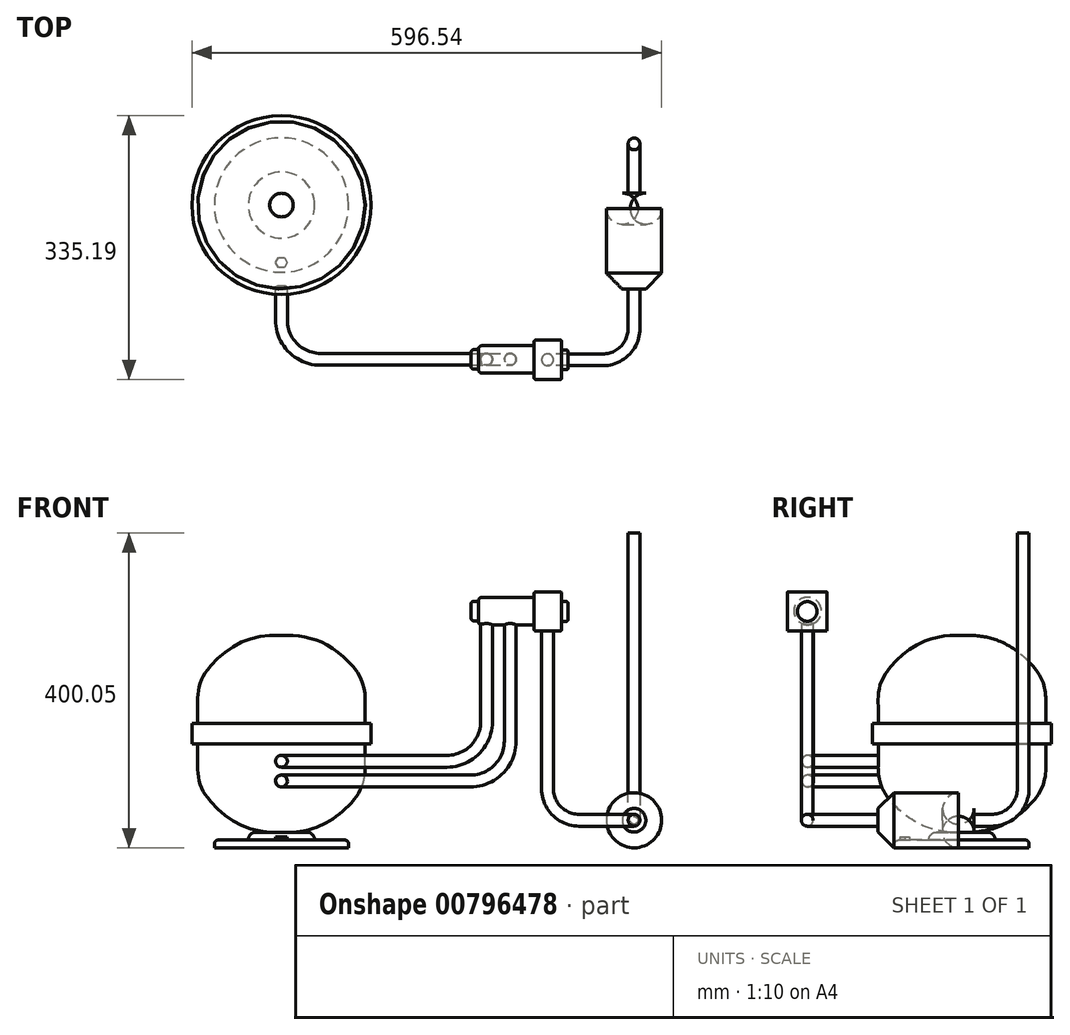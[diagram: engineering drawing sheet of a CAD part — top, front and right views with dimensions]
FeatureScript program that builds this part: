
annotation { "Feature Type Name" : "Feature", "Feature Type Description" : "" }
export const myFeature = defineFeature(function(context is Context, id is Id, definition is map)
    precondition{}
    {
        {
            var Q0;
            Q0=qCreatedBy(makeId("Front.planeOp"),FACE);
            var sketch = newSketch(context, id + "F0", { "sketchPlane" : qUnion([Q0])});
            skLineSegment(sketch, "E0", {"start": v(0, 125) * mm, "end": v(0, 0) * mm});
            skLineSegment(sketch, "E1", {"start": v(0, 125) * mm, "end": v(15, 125) * mm});
            skFitSpline(sketch, "E2", {"points": [v(15, 125) * mm, v(59.48, 111.76) * mm, v(101.6, 68.43) * mm, v(106.42, 35.93) * mm, v(106.42, 13.06) * mm], "startDerivative": vector(170.56, -15.33) * mm, "endDerivative": vector(0, -154.1) * mm});
            skLineSegment(sketch, "E3", {"start": v(106.42, 13.06) * mm, "end": v(113.64, 13.06) * mm});
            skLineSegment(sketch, "E4", {"start": v(113.64, 13.06) * mm, "end": v(113.64, 0) * mm});
            skLineSegment(sketch, "E5", {"start": v(0, 0) * mm, "end": v(113.64, 0) * mm});
            skFitSpline(sketch, "E6.MirrorCS", {"points": [v(15, -125) * mm, v(59.48, -111.76) * mm, v(101.6, -68.43) * mm, v(106.42, -35.93) * mm, v(106.42, -13.06) * mm], "startDerivative": vector(170.56, 15.33) * mm, "endDerivative": vector(0, 154.1) * mm});
            skLineSegment(sketch, "E7.MirrorCS", {"start": v(0, -125) * mm, "end": v(15, -125) * mm});
            skLineSegment(sketch, "E8.MirrorCS", {"start": v(0, -125) * mm, "end": v(0, 0) * mm});
            skLineSegment(sketch, "E9.MirrorCS", {"start": v(106.42, -13.06) * mm, "end": v(113.64, -13.06) * mm});
            skLineSegment(sketch, "E10.MirrorCS", {"start": v(113.64, -13.06) * mm, "end": v(113.64, 0) * mm});
            skPoint(sketch, "E11.MirrorCS.start.orphan", {"position": v(-15, 125) * mm});
            skPoint(sketch, "E12.MirrorCS.start.orphan", {"position": v(0, 125) * mm});
            skSolve(sketch);
        }
        {
            var Q0;
            Q0=makeQuery(id+"F0.imprint","IMPRINT",FACE,{"disambiguationData":[TD([[makeQuery(id+"F0.imprint","IMPRINT",EDGE,{"derivedFrom":sQuery(id+"F0.wireOp",EDGE,"E0")}),1.0]])]});
            var Q1;
            Q1=makeQuery(id+"F0.imprint","IMPRINT",FACE,{"disambiguationData":[TD([[makeQuery(id+"F0.imprint","IMPRINT",EDGE,{"derivedFrom":sQuery(id+"F0.wireOp",EDGE,"E5")}),-1.0]])]});
            var Q2;
            Q2=sQuery(id+"F0.wireOp",EDGE,"E0");
            revolve(context, id + "F1", {"surfaceOperationType" : NewSurfaceOperationType.NEW, "entities" : qUnion([Q0, Q1]), "axis" : qUnion([Q2]), "revolveType" : RevolveType.FULL});
        }
        {
            var Q0;
            Q0=makeQuery(id+"F1.opRevolve","SWEPT_FACE",FACE,{"disambiguationData":[OSD([sQuery(id+"F0.wireOp",EDGE,"E7.MirrorCS")])]});
            var sketch = newSketch(context, id + "F2", { "sketchPlane" : qUnion([Q0])});
            skCircle(sketch, "E13", {"center": v(0, 0) * mm, "radius": 42.2 * mm});
            skSolve(sketch);
        }
        {
            var Q0;
            Q0 = qSketchRegion(id + "F2", true);
            extrude(context, id + "F3", {"entities" : qUnion([Q0]), "operationType" : NewBodyOperationType.ADD, "depth" : 10 * mm, "offsetDistance" : 25 * mm});
        }
        {
            var Q0;
            Q0=makeQuery(id+"F3.opExtrude","CAP_FACE",FACE,{"disambiguationData":[OSD([sQuery(id+"F2.wireOp",EDGE,"E13")])],"isStart":false});
            var sketch = newSketch(context, id + "F4", { "sketchPlane" : qUnion([Q0])});
            skCircle(sketch, "E14", {"center": v(0, 0) * mm, "radius": 85.28 * mm});
            skSolve(sketch);
        }
        {
            var Q0;
            Q0 = qSketchRegion(id + "F4", true);
            extrude(context, id + "F5", {"entities" : qUnion([Q0]), "operationType" : NewBodyOperationType.ADD, "depth" : 10 * mm, "offsetDistance" : 25 * mm});
        }
        {
            var Q0;
            Q0=makeQuery(id+"F3.opExtrude","CAP_EDGE",EDGE,{"disambiguationData":[OSD([sQuery(id+"F2.wireOp",EDGE,"E13")])],"isStart":false});
            var Q1;
            Q1=makeQuery(id+"F5.opExtrude","CAP_EDGE",EDGE,{"disambiguationData":[OSD([sQuery(id+"F4.wireOp",EDGE,"E14")])],"isStart":true});
            fillet(context, id + "F6", {"entities" : qUnion([Q0, Q1]), "radius" : 5 * mm, "tangentPropagation" : true, "allowEdgeOverflow" : false});
        }
        {
            var Q0;
            Q0=makeQuery(id+"F3.opExtrude","CAP_EDGE",EDGE,{"disambiguationData":[OSD([sQuery(id+"F2.wireOp",EDGE,"E13")])],"isStart":true});
            fillet(context, id + "F7", {"entities" : qUnion([Q0]), "radius" : 10 * mm, "tangentPropagation" : true, "allowEdgeOverflow" : false});
        }
        {
            var Q0;
            Q0=makeQuery(id+"F5.opExtrude","CAP_FACE",FACE,{"disambiguationData":[OSD([sQuery(id+"F4.wireOp",EDGE,"E14")])],"isStart":true});
            var sketch = newSketch(context, id + "F8", { "sketchPlane" : qUnion([Q0])});
            skCircle(sketch, "E15.cCircle", {"center": v(0, -72.8) * mm, "radius": 6.33 * mm, "construction": true});
            skLineSegment(sketch, "E15.0", {"start": v(-3.65, -66.47) * mm, "end": v(3.65, -66.47) * mm});
            skLineSegment(sketch, "E15.1", {"start": v(3.65, -66.47) * mm, "end": v(7.3, -72.8) * mm});
            skLineSegment(sketch, "E15.2", {"start": v(7.3, -72.8) * mm, "end": v(3.65, -79.13) * mm});
            skLineSegment(sketch, "E15.3", {"start": v(3.65, -79.13) * mm, "end": v(-3.65, -79.13) * mm});
            skLineSegment(sketch, "E15.4", {"start": v(-3.65, -79.13) * mm, "end": v(-7.3, -72.8) * mm});
            skLineSegment(sketch, "E15.5", {"start": v(-7.3, -72.8) * mm, "end": v(-3.65, -66.47) * mm});
            skPoint(sketch, "E15.0.midPoint", {"position": v(0, -66.47) * mm});
            skSolve(sketch);
        }
        {
            var Q0;
            Q0 = qSketchRegion(id + "F8", true);
            extrude(context, id + "F9", {"entities" : qUnion([Q0]), "operationType" : NewBodyOperationType.ADD, "depth" : 4 * mm, "offsetDistance" : 25 * mm});
        }
        {
            var Q0;
            Q0=qCreatedBy(makeId("Front.planeOp"),FACE);
            cPlane(context, id + "F10", {"entities" : qUnion([Q0]), "cplaneType" : CPlaneType.OFFSET, "offset" : 100 * mm, "width" : 150 * mm, "height" : 150 * mm});
        }
        {
            var Q0;
            Q0=qCreatedBy(id+"F10.planeOp",FACE);
            var sketch = newSketch(context, id + "F11", { "sketchPlane" : qUnion([Q0])});
            skCircle(sketch, "E16", {"center": v(0, -35) * mm, "radius": 7.5 * mm});
            skCircle(sketch, "E17", {"center": v(0, -60) * mm, "radius": 7.5 * mm});
            skSolve(sketch);
        }
        {
            var Q0;
            Q0 = qSketchRegion(id + "F11", true);
            extrude(context, id + "F12", {"entities" : qUnion([Q0]), "operationType" : NewBodyOperationType.ADD, "depth" : 46 * mm, "offsetDistance" : 25 * mm});
        }
        {
            var Q0;
            Q0=makeQuery(id+"F5.opExtrude","CAP_FACE",FACE,{"disambiguationData":[OSD([sQuery(id+"F4.wireOp",EDGE,"E14")])],"isStart":false});
            cPlane(context, id + "F13", {"entities" : qUnion([Q0]), "cplaneType" : CPlaneType.OFFSET, "offset" : 85 * mm, "oppositeDirection" : true, "width" : 150 * mm, "height" : 150 * mm});
        }
        {
            var Q0;
            Q0=qCreatedBy(id+"F13.planeOp",FACE);
            var sketch = newSketch(context, id + "F14", { "sketchPlane" : qUnion([Q0])});
            skLineSegment(sketch, "E18", {"start": v(0, 146) * mm, "end": v(0, 146) * mm});
            skLineSegment(sketch, "E19", {"start": v(50, 196) * mm, "end": v(240, 196) * mm});
            skPoint(sketch, "E20.visualSharp", {"position": v(0, 196) * mm});
            skArc(sketch, "E20.filletArc", {"start": v(50, 196) * mm, "mid": v(14.64, 181.36) * mm, "end": v(0, 146) * mm});
            skSolve(sketch);
        }
        {
            var Q0;
            Q0=makeQuery(id+"F12.opExtrude","CAP_FACE",FACE,{"disambiguationData":[OSD([sQuery(id+"F11.wireOp",EDGE,"E17")])],"isStart":false});
            var Q1;
            Q1=sQuery(id+"F14.wireOp",EDGE,"E19");
            var Q2;
            Q2=sQuery(id+"F14.wireOp",EDGE,"E20.filletArc");
            sweep(context, id + "F15", {"operationType" : NewBodyOperationType.ADD, "profiles" : qUnion([Q0]), "path" : qUnion([Q1, Q2])});
        }
        {
            var Q0;
            Q0=qCreatedBy(id+"F13.planeOp",FACE);
            cPlane(context, id + "F16", {"entities" : qUnion([Q0]), "cplaneType" : CPlaneType.OFFSET, "offset" : 25 * mm, "oppositeDirection" : true, "width" : 150 * mm, "height" : 150 * mm});
        }
        {
            var Q0;
            Q0=qCreatedBy(id+"F16.planeOp",FACE);
            var sketch = newSketch(context, id + "F17", { "sketchPlane" : qUnion([Q0])});
            skLineSegment(sketch, "E21", {"start": v(50, 196) * mm, "end": v(210, 196) * mm});
            skPoint(sketch, "E22.visualSharp", {"position": v(0, 196) * mm});
            skArc(sketch, "E22.filletArc", {"start": v(50, 196) * mm, "mid": v(14.64, 181.36) * mm, "end": v(0, 146) * mm});
            skSolve(sketch);
        }
        {
            var Q0;
            Q0=makeQuery(id+"F12.opExtrude","CAP_FACE",FACE,{"disambiguationData":[OSD([sQuery(id+"F11.wireOp",EDGE,"E16")])],"isStart":false});
            var Q1;
            Q1=makeQuery(id+"F12.opExtrude","CAP_EDGE",EDGE,{"disambiguationData":[OSD([sQuery(id+"F11.wireOp",EDGE,"E16")])],"isStart":false});
            var Q2;
            Q2=sQuery(id+"F17.wireOp",EDGE,"E22.filletArc");
            var Q3;
            Q3=sQuery(id+"F17.wireOp",EDGE,"E21");
            sweep(context, id + "F18", {"operationType" : NewBodyOperationType.ADD, "profiles" : qUnion([Q0]), "surfaceProfiles" : qUnion([Q1]), "path" : qUnion([Q2, Q3])});
        }
        {
            var Q0;
            Q0=qCreatedBy(id+"F10.planeOp",FACE);
            cPlane(context, id + "F19", {"entities" : qUnion([Q0]), "cplaneType" : CPlaneType.OFFSET, "offset" : 95 * mm, "width" : 150 * mm, "height" : 150 * mm});
        }
        {
            var Q0;
            Q0=qCreatedBy(id+"F19.planeOp",FACE);
            var sketch = newSketch(context, id + "F20", { "sketchPlane" : qUnion([Q0])});
            skLineSegment(sketch, "E23", {"start": v(210, -34.56) * mm, "end": v(210, -34.56) * mm});
            skLineSegment(sketch, "E24", {"start": v(260, 15.44) * mm, "end": v(260, 155.44) * mm});
            skPoint(sketch, "E25.visualSharp", {"position": v(260, -34.56) * mm});
            skArc(sketch, "E25.filletArc", {"start": v(210, -34.56) * mm, "mid": v(245.36, -19.92) * mm, "end": v(260, 15.44) * mm});
            skSolve(sketch);
        }
        {
            var Q0;
            Q0=makeQuery(id+"F18.opSweep","CAP_FACE",FACE,{"disambiguationData":[OSD([sQuery(id+"F11.wireOp",EDGE,"E16"),sQuery(id+"F17.wireOp",VERTEX,"E21.end")])],"isStart":false});
            var Q1;
            Q1=sQuery(id+"F20.wireOp",EDGE,"E25.filletArc");
            var Q2;
            Q2=sQuery(id+"F20.wireOp",EDGE,"E24");
            sweep(context, id + "F21", {"operationType" : NewBodyOperationType.ADD, "profiles" : qUnion([Q0]), "path" : qUnion([Q1, Q2])});
        }
        {
            var Q0;
            Q0=qCreatedBy(id+"F19.planeOp",FACE);
            var sketch = newSketch(context, id + "F22", { "sketchPlane" : qUnion([Q0])});
            skLineSegment(sketch, "E26", {"start": v(240, -59.4) * mm, "end": v(240, -59.4) * mm});
            skLineSegment(sketch, "E27", {"start": v(290, -9.4) * mm, "end": v(290, 154.4) * mm});
            skPoint(sketch, "E28.visualSharp", {"position": v(290, -59.4) * mm});
            skArc(sketch, "E28.filletArc", {"start": v(240, -59.4) * mm, "mid": v(275.36, -44.76) * mm, "end": v(290, -9.4) * mm});
            skSolve(sketch);
        }
        {
            var Q0;
            Q0=makeQuery(id+"F15.opSweep","CAP_FACE",FACE,{"disambiguationData":[OSD([sQuery(id+"F11.wireOp",EDGE,"E17"),sQuery(id+"F14.wireOp",VERTEX,"E19.end")])],"isStart":false});
            var Q1;
            Q1=sQuery(id+"F22.wireOp",EDGE,"E28.filletArc");
            var Q2;
            Q2=sQuery(id+"F22.wireOp",EDGE,"E27");
            sweep(context, id + "F23", {"operationType" : NewBodyOperationType.ADD, "profiles" : qUnion([Q0]), "path" : qUnion([Q1, Q2])});
        }
        {
            var Q0;
            Q0=qCreatedBy(makeId("Right.planeOp"),FACE);
            cPlane(context, id + "F24", {"entities" : qUnion([Q0]), "cplaneType" : CPlaneType.OFFSET, "offset" : 250 * mm, "width" : 150 * mm, "height" : 150 * mm});
        }
        {
            var Q0;
            Q0=qCreatedBy(id+"F24.planeOp",FACE);
            var sketch = newSketch(context, id + "F25", { "sketchPlane" : qUnion([Q0])});
            skCircle(sketch, "E29", {"center": v(-196.05, 155.9) * mm, "radius": 17.5 * mm});
            skSolve(sketch);
        }
        {
            var Q0;
            Q0 = qSketchRegion(id + "F25", true);
            extrude(context, id + "F26", {"entities" : qUnion([Q0]), "operationType" : NewBodyOperationType.ADD, "depth" : 71 * mm, "offsetDistance" : 25 * mm});
        }
        {
            var Q0;
            Q0=makeQuery(id+"F26.opExtrude","CAP_FACE",FACE,{"disambiguationData":[OSD([sQuery(id+"F25.wireOp",EDGE,"E29")])],"isStart":true});
            var sketch = newSketch(context, id + "F27", { "sketchPlane" : qUnion([Q0])});
            skCircle(sketch, "E30", {"center": v(196.05, 155.9) * mm, "radius": 12.38 * mm});
            skSolve(sketch);
        }
        {
            var Q0;
            Q0 = qSketchRegion(id + "F27", true);
            extrude(context, id + "F28", {"entities" : qUnion([Q0]), "operationType" : NewBodyOperationType.ADD, "depth" : 9 * mm, "offsetDistance" : 25 * mm});
        }
        {
            var Q0;
            Q0=makeQuery(id+"F28.opExtrude","CAP_EDGE",EDGE,{"disambiguationData":[OSD([sQuery(id+"F27.wireOp",EDGE,"E30")])],"isStart":false});
            fillet(context, id + "F29", {"entities" : qUnion([Q0]), "radius" : 3 * mm, "tangentPropagation" : true, "allowEdgeOverflow" : false});
        }
        {
            var Q0;
            Q0=makeQuery(id+"F26.opExtrude","CAP_EDGE",EDGE,{"disambiguationData":[OSD([sQuery(id+"F25.wireOp",EDGE,"E29")])],"isStart":true});
            fillet(context, id + "F30", {"entities" : qUnion([Q0]), "radius" : 5 * mm, "tangentPropagation" : true, "allowEdgeOverflow" : false});
        }
        {
            var Q0;
            Q0=makeQuery(id+"F26.opExtrude","CAP_FACE",FACE,{"disambiguationData":[OSD([sQuery(id+"F25.wireOp",EDGE,"E29")])],"isStart":false});
            var sketch = newSketch(context, id + "F31", { "sketchPlane" : qUnion([Q0])});
            skLineSegment(sketch, "E31.bottom", {"start": v(-221.55, 180.4) * mm, "end": v(-171.55, 180.4) * mm});
            skLineSegment(sketch, "E31.top", {"start": v(-221.55, 130.4) * mm, "end": v(-171.55, 130.4) * mm});
            skLineSegment(sketch, "E31.left", {"start": v(-221.55, 180.4) * mm, "end": v(-221.55, 130.4) * mm});
            skLineSegment(sketch, "E31.right", {"start": v(-171.55, 180.4) * mm, "end": v(-171.55, 130.4) * mm});
            skSolve(sketch);
        }
        {
            var Q0;
            Q0 = qSketchRegion(id + "F31", true);
            extrude(context, id + "F32", {"entities" : qUnion([Q0]), "operationType" : NewBodyOperationType.ADD, "depth" : 35 * mm, "offsetDistance" : 25 * mm});
        }
        {
            var Q0;
            Q0=makeQuery(id+"F32.opExtrude","CAP_FACE",FACE,{"disambiguationData":[OSD([sQuery(id+"F31.wireOp",EDGE,"E31.bottom"),sQuery(id+"F31.wireOp",EDGE,"E31.top"),sQuery(id+"F31.wireOp",EDGE,"E31.left"),sQuery(id+"F31.wireOp",EDGE,"E31.right")])],"isStart":false});
            var sketch = newSketch(context, id + "F33", { "sketchPlane" : qUnion([Q0])});
            skCircle(sketch, "E32", {"center": v(-196.55, 155.4) * mm, "radius": 12.5 * mm});
            skSolve(sketch);
        }
        {
            var Q0;
            Q0 = qSketchRegion(id + "F33", true);
            extrude(context, id + "F34", {"entities" : qUnion([Q0]), "operationType" : NewBodyOperationType.ADD, "depth" : 7.9 * mm, "offsetDistance" : 25 * mm});
        }
        {
            var Q0;
            Q0=makeQuery(id+"F32.opExtrude","CAP_EDGE",EDGE,{"disambiguationData":[OSD([sQuery(id+"F31.wireOp",EDGE,"E31.left")])],"isStart":false});
            var Q1;
            Q1=makeQuery(id+"F32.opExtrude","CAP_EDGE",EDGE,{"disambiguationData":[OSD([sQuery(id+"F31.wireOp",EDGE,"E31.bottom")])],"isStart":false});
            var Q2;
            Q2=makeQuery(id+"F32.opExtrude","CAP_EDGE",EDGE,{"disambiguationData":[OSD([sQuery(id+"F31.wireOp",EDGE,"E31.right")])],"isStart":false});
            var Q3;
            Q3=makeQuery(id+"F32.opExtrude","CAP_EDGE",EDGE,{"disambiguationData":[OSD([sQuery(id+"F31.wireOp",EDGE,"E31.top")])],"isStart":false});
            var Q4;
            Q4=makeQuery(id+"F32.opExtrude","CAP_EDGE",EDGE,{"disambiguationData":[OSD([sQuery(id+"F31.wireOp",EDGE,"E31.left")])],"isStart":true});
            var Q5;
            Q5=makeQuery(id+"F32.opExtrude","CAP_EDGE",EDGE,{"disambiguationData":[OSD([sQuery(id+"F31.wireOp",EDGE,"E31.bottom")])],"isStart":true});
            var Q6;
            Q6=makeQuery(id+"F32.opExtrude","CAP_EDGE",EDGE,{"disambiguationData":[OSD([sQuery(id+"F31.wireOp",EDGE,"E31.right")])],"isStart":true});
            var Q7;
            Q7=makeQuery(id+"F32.opExtrude","CAP_EDGE",EDGE,{"disambiguationData":[OSD([sQuery(id+"F31.wireOp",EDGE,"E31.top")])],"isStart":true});
            var Q8;
            Q8=makeQuery(id+"F34.opExtrude","CAP_EDGE",EDGE,{"disambiguationData":[OSD([sQuery(id+"F33.wireOp",EDGE,"E32")])],"isStart":false});
            fillet(context, id + "F35", {"entities" : qUnion([Q0, Q1, Q2, Q3, Q4, Q5, Q6, Q7, Q8]), "radius" : 2 * mm, "tangentPropagation" : true, "allowEdgeOverflow" : false});
        }
        {
            var Q0;
            Q0=makeQuery(id+"F32.opExtrude","SWEPT_FACE",FACE,{"disambiguationData":[OSD([sQuery(id+"F31.wireOp",EDGE,"E31.top")])]});
            var sketch = newSketch(context, id + "F36", { "sketchPlane" : qUnion([Q0])});
            skCircle(sketch, "E33", {"center": v(338, 196.55) * mm, "radius": 7.5 * mm});
            skSolve(sketch);
        }
        {
            var Q0;
            Q0 = qSketchRegion(id + "F36", true);
            extrude(context, id + "F37", {"entities" : qUnion([Q0]), "operationType" : NewBodyOperationType.ADD, "depth" : 200.3 * mm, "offsetDistance" : 25 * mm});
        }
        {
            var Q0;
            Q0=qCreatedBy(id+"F19.planeOp",FACE);
            var sketch = newSketch(context, id + "F38", { "sketchPlane" : qUnion([Q0])});
            skLineSegment(sketch, "E34", {"start": v(378, -109.9) * mm, "end": v(408, -109.9) * mm});
            skPoint(sketch, "E35.visualSharp", {"position": v(338, -109.9) * mm});
            skArc(sketch, "E35.filletArc", {"start": v(338, -69.9) * mm, "mid": v(349.72, -98.19) * mm, "end": v(378, -109.9) * mm});
            skSolve(sketch);
        }
        {
            var Q0;
            Q0=makeQuery(id+"F37.opExtrude","CAP_FACE",FACE,{"disambiguationData":[OSD([sQuery(id+"F36.wireOp",EDGE,"E33")])],"isStart":false});
            var Q1;
            Q1=sQuery(id+"F38.wireOp",EDGE,"E35.filletArc");
            var Q2;
            Q2=sQuery(id+"F38.wireOp",EDGE,"E34");
            sweep(context, id + "F39", {"operationType" : NewBodyOperationType.ADD, "profiles" : qUnion([Q0]), "path" : qUnion([Q1, Q2])});
        }
        {
            var Q0;
            Q0=qCreatedBy(makeId("Top.planeOp"),FACE);
            cPlane(context, id + "F40", {"entities" : qUnion([Q0]), "cplaneType" : CPlaneType.OFFSET, "offset" : 90 * mm, "oppositeDirection" : true, "width" : 150 * mm, "height" : 150 * mm});
        }
        {
            var Q0;
            Q0=qCreatedBy(id+"F40.planeOp",FACE);
            var sketch = newSketch(context, id + "F41", { "sketchPlane" : qUnion([Q0])});
            skLineSegment(sketch, "E36", {"start": v(448, -156.65) * mm, "end": v(448, -106.65) * mm});
            skPoint(sketch, "E37.visualSharp", {"position": v(448, -196.65) * mm});
            skArc(sketch, "E37.filletArc", {"start": v(408, -196.65) * mm, "mid": v(436.28, -184.94) * mm, "end": v(448, -156.65) * mm});
            skSolve(sketch);
        }
        {
            var Q0;
            Q0=makeQuery(id+"F39.opSweep","CAP_FACE",FACE,{"disambiguationData":[OSD([sQuery(id+"F36.wireOp",EDGE,"E33"),sQuery(id+"F38.wireOp",VERTEX,"E34.end")])],"isStart":false});
            var Q1;
            Q1=sQuery(id+"F41.wireOp",EDGE,"E37.filletArc");
            var Q2;
            Q2=sQuery(id+"F41.wireOp",EDGE,"E36");
            sweep(context, id + "F42", {"operationType" : NewBodyOperationType.ADD, "profiles" : qUnion([Q0]), "path" : qUnion([Q1, Q2])});
        }
        {
            var Q0;
            Q0=makeQuery(id+"F42.opSweep","CAP_FACE",FACE,{"disambiguationData":[OSD([sQuery(id+"F36.wireOp",EDGE,"E33"),sQuery(id+"F38.wireOp",VERTEX,"E34.end"),sQuery(id+"F41.wireOp",VERTEX,"E36.end")])],"isStart":false});
            var sketch = newSketch(context, id + "F43", { "sketchPlane" : qUnion([Q0])});
            skCircle(sketch, "E38", {"center": v(-447.9, -109.9) * mm, "radius": 35 * mm});
            skSolve(sketch);
        }
        {
            var Q0;
            Q0 = qSketchRegion(id + "F43", true);
            extrude(context, id + "F44", {"entities" : qUnion([Q0]), "operationType" : NewBodyOperationType.ADD, "depth" : 122 * mm, "offsetDistance" : 25 * mm});
        }
        {
            var Q0;
            Q0=makeQuery(id+"F44.opExtrude","CAP_EDGE",EDGE,{"disambiguationData":[OSD([sQuery(id+"F43.wireOp",EDGE,"E38")])],"isStart":true});
            chamfer(context, id + "F45", {"entities" : qUnion([Q0]), "width" : 20 * mm, "tangentPropagation" : true});
        }
        {
            var Q0;
            Q0=makeQuery(id+"F44.opExtrude","CAP_EDGE",EDGE,{"disambiguationData":[OSD([sQuery(id+"F43.wireOp",EDGE,"E38")])],"isStart":false});
            fillet(context, id + "F46", {"entities" : qUnion([Q0]), "radius" : 20 * mm, "tangentPropagation" : true, "allowEdgeOverflow" : false});
        }
        {
            var Q0;
            Q0=qCreatedBy(makeId("Right.planeOp"),FACE);
            cPlane(context, id + "F47", {"entities" : qUnion([Q0]), "cplaneType" : CPlaneType.OFFSET, "offset" : 450 * mm, "width" : 150 * mm, "height" : 150 * mm});
        }
        {
            var Q0;
            Q0=makeQuery(id+"F44.opExtrude","CAP_FACE",FACE,{"disambiguationData":[OSD([sQuery(id+"F43.wireOp",EDGE,"E38")])],"isStart":false});
            var sketch = newSketch(context, id + "F48", { "sketchPlane" : qUnion([Q0])});
            skCircle(sketch, "E39", {"center": v(-447.9, -109.9) * mm, "radius": 7.5 * mm});
            skSolve(sketch);
        }
        {
            var Q0;
            Q0=qCreatedBy(id+"F47.planeOp",FACE);
            var sketch = newSketch(context, id + "F49", { "sketchPlane" : qUnion([Q0])});
            skLineSegment(sketch, "E40", {"start": v(15.52, -109.77) * mm, "end": v(37.57, -109.77) * mm});
            skLineSegment(sketch, "E41", {"start": v(77.57, -69.77) * mm, "end": v(77.57, 255.23) * mm});
            skPoint(sketch, "E42.visualSharp", {"position": v(77.57, -109.77) * mm});
            skArc(sketch, "E42.filletArc", {"start": v(37.57, -109.77) * mm, "mid": v(65.85, -98.06) * mm, "end": v(77.57, -69.77) * mm});
            skSolve(sketch);
        }
        {
            var Q0;
            Q0=makeQuery(id+"F48.imprint","IMPRINT",FACE,{"disambiguationData":[TD([[makeQuery(id+"F48.imprint","IMPRINT",EDGE,{"derivedFrom":sQuery(id+"F48.wireOp",EDGE,"E39")}),1.0]])]});
            var Q1;
            Q1=sQuery(id+"F49.wireOp",EDGE,"E40");
            var Q2;
            Q2=sQuery(id+"F49.wireOp",EDGE,"E42.filletArc");
            var Q3;
            Q3=sQuery(id+"F49.wireOp",EDGE,"E41");
            sweep(context, id + "F50", {"operationType" : NewBodyOperationType.ADD, "profiles" : qUnion([Q0]), "path" : qUnion([Q1, Q2, Q3])});
        }
    });
